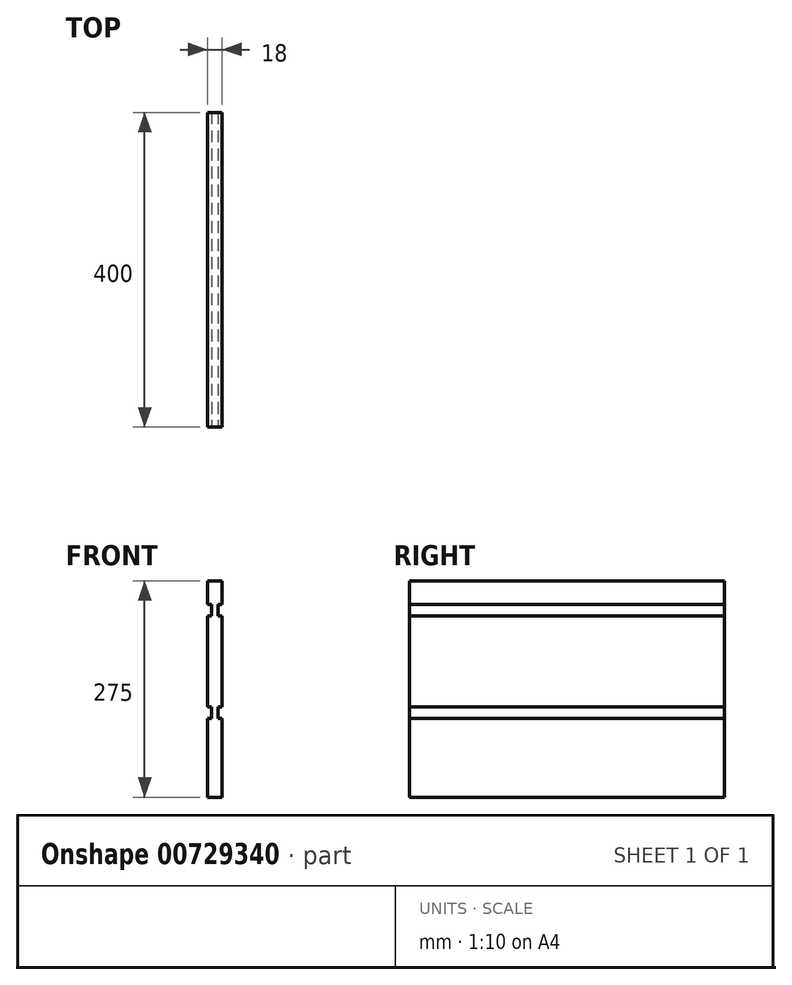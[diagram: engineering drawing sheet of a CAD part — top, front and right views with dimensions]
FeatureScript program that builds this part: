
annotation { "Feature Type Name" : "Feature", "Feature Type Description" : "" }
export const myFeature = defineFeature(function(context is Context, id is Id, definition is map)
    precondition{}
    {
        {
            var Q0;
            Q0=qCreatedBy(makeId("Front.planeOp"),FACE);
            var sketch = newSketch(context, id + "F0", { "sketchPlane" : qUnion([Q0])});
            skLineSegment(sketch, "E0.bottom", {"start": v(0, 0) * mm, "end": v(18, 0) * mm});
            skLineSegment(sketch, "E0.top", {"start": v(0, 275) * mm, "end": v(18, 275) * mm});
            skLineSegment(sketch, "E0.left", {"start": v(0, 0) * mm, "end": v(0, 275) * mm});
            skLineSegment(sketch, "E0.right", {"start": v(18, 0) * mm, "end": v(18, 275) * mm});
            skSolve(sketch);
        }
        {
            var Q0;
            Q0 = qSketchRegion(id + "F0", true);
            extrude(context, id + "F1", {"entities" : qUnion([Q0]), "oppositeDirection" : true, "depth" : 400 * mm, "offsetDistance" : 25 * mm});
        }
        {
            var Q0;
            Q0=makeQuery(id+"F1.opExtrude","CAP_FACE",FACE,{"disambiguationData":[OSD([sQuery(id+"F0.wireOp",EDGE,"E0.bottom"),sQuery(id+"F0.wireOp",EDGE,"E0.top"),sQuery(id+"F0.wireOp",EDGE,"E0.left"),sQuery(id+"F0.wireOp",EDGE,"E0.right")])],"isStart":true});
            var sketch = newSketch(context, id + "F2", { "sketchPlane" : qUnion([Q0])});
            skLineSegment(sketch, "E1", {"start": v(9, 275) * mm, "end": v(9, 0) * mm, "construction": true});
            skLineSegment(sketch, "E2.bottom", {"start": v(18, 245) * mm, "end": v(13, 245) * mm});
            skLineSegment(sketch, "E2.top", {"start": v(18, 230) * mm, "end": v(13, 230) * mm});
            skLineSegment(sketch, "E2.left", {"start": v(18, 245) * mm, "end": v(18, 230) * mm});
            skLineSegment(sketch, "E2.right", {"start": v(13, 245) * mm, "end": v(13, 230) * mm});
            skLineSegment(sketch, "E3.bottom", {"start": v(18, 115) * mm, "end": v(13, 115) * mm});
            skLineSegment(sketch, "E3.top", {"start": v(18, 100) * mm, "end": v(13, 100) * mm});
            skLineSegment(sketch, "E3.left", {"start": v(18, 115) * mm, "end": v(18, 100) * mm});
            skLineSegment(sketch, "E3.right", {"start": v(13, 115) * mm, "end": v(13, 100) * mm});
            skLineSegment(sketch, "E4.MirrorCS", {"start": v(0, 245) * mm, "end": v(5, 245) * mm});
            skLineSegment(sketch, "E5.MirrorCS", {"start": v(0, 230) * mm, "end": v(5, 230) * mm});
            skLineSegment(sketch, "E6.MirrorCS", {"start": v(0, 245) * mm, "end": v(0, 230) * mm});
            skLineSegment(sketch, "E7.MirrorCS", {"start": v(5, 245) * mm, "end": v(5, 230) * mm});
            skLineSegment(sketch, "E8.MirrorCS", {"start": v(0, 100) * mm, "end": v(5, 100) * mm});
            skLineSegment(sketch, "E9.MirrorCS", {"start": v(0, 115) * mm, "end": v(5, 115) * mm});
            skLineSegment(sketch, "E10.MirrorCS", {"start": v(0, 115) * mm, "end": v(0, 100) * mm});
            skLineSegment(sketch, "E11.MirrorCS", {"start": v(5, 115) * mm, "end": v(5, 100) * mm});
            skSolve(sketch);
        }
        {
            var Q0;
            Q0 = qSketchRegion(id + "F2", true);
            extrude(context, id + "F3", {"entities" : qUnion([Q0]), "operationType" : NewBodyOperationType.REMOVE, "endBound" : BoundingType.THROUGH_ALL, "oppositeDirection" : true, "depth" : 25 * mm, "offsetDistance" : 25 * mm});
        }
    });
